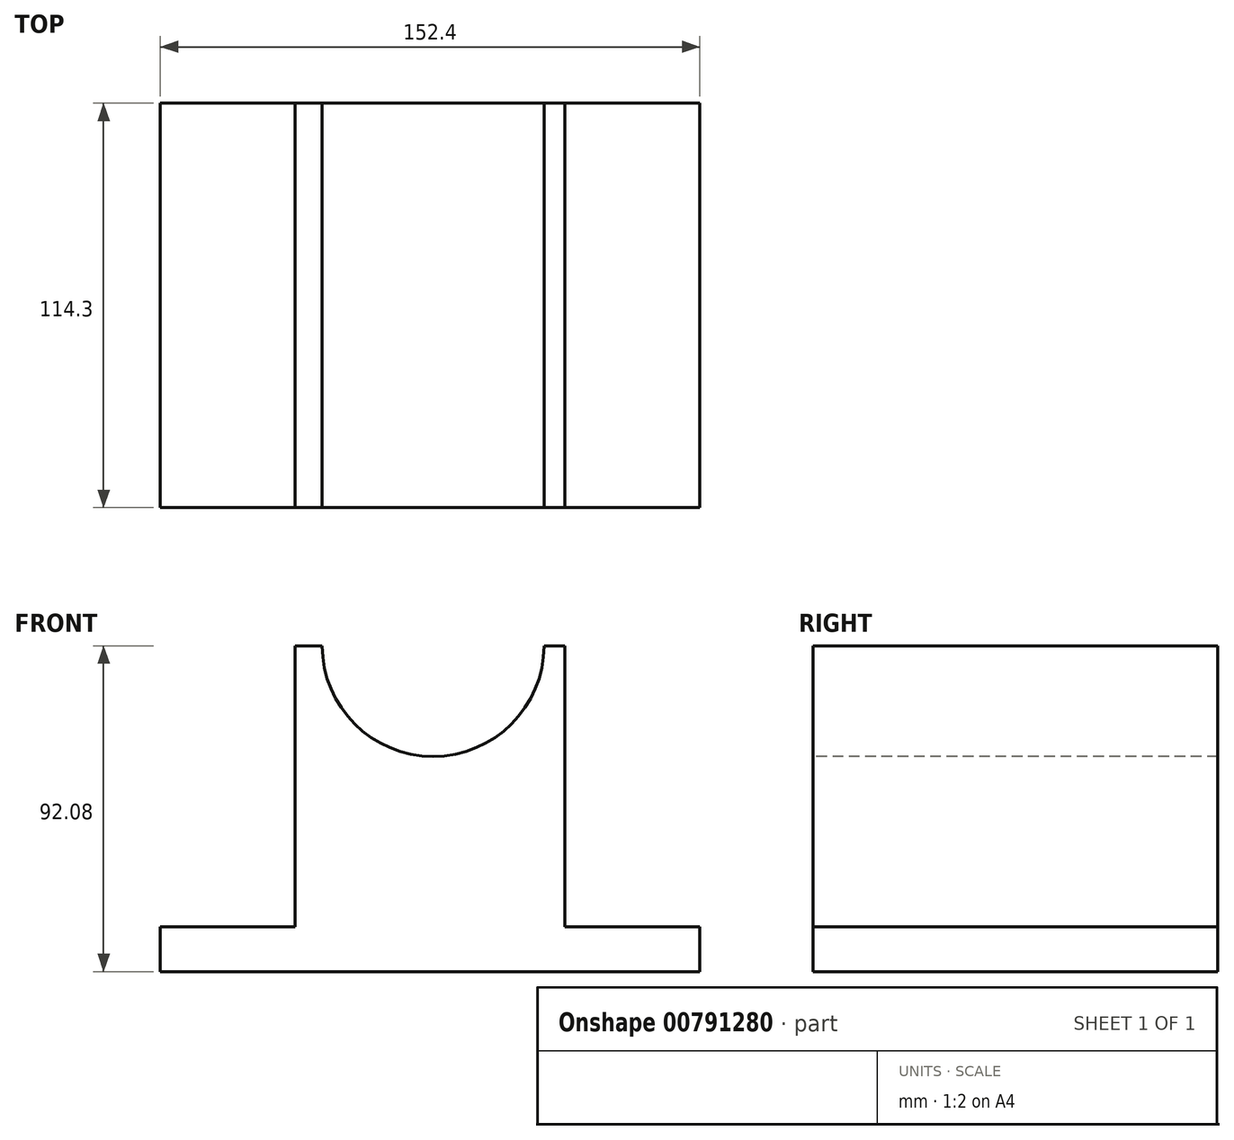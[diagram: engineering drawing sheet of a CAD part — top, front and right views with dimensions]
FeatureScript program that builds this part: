
annotation { "Feature Type Name" : "Feature", "Feature Type Description" : "" }
export const myFeature = defineFeature(function(context is Context, id is Id, definition is map)
    precondition{}
    {
        {
            var Q0;
            Q0=qCreatedBy(makeId("Front.planeOp"),FACE);
            var sketch = newSketch(context, id + "F0", { "sketchPlane" : qUnion([Q0])});
            skLineSegment(sketch, "E0", {"start": v(0, 0) * mm, "end": v(152.4, 0) * mm});
            skLineSegment(sketch, "E1", {"start": v(152.4, 0) * mm, "end": v(152.4, 12.7) * mm});
            skLineSegment(sketch, "E2", {"start": v(152.4, 12.7) * mm, "end": v(114.3, 12.7) * mm});
            skLineSegment(sketch, "E3", {"start": v(114.3, 12.7) * mm, "end": v(114.3, 92.08) * mm});
            skLineSegment(sketch, "E4", {"start": v(114.3, 92.08) * mm, "end": v(38.1, 92.08) * mm});
            skLineSegment(sketch, "E5", {"start": v(38.1, 92.08) * mm, "end": v(38.1, 12.7) * mm});
            skLineSegment(sketch, "E6", {"start": v(38.1, 12.7) * mm, "end": v(0, 12.7) * mm});
            skLineSegment(sketch, "E7", {"start": v(0, 12.7) * mm, "end": v(0, 0) * mm});
            skSolve(sketch);
        }
        {
            var Q0;
            Q0 = qSketchRegion(id + "F0", true);
            extrude(context, id + "F1", {"entities" : qUnion([Q0]), "depth" : 114.3 * mm, "offsetDistance" : 25.4 * mm});
        }
        {
            var Q0;
            Q0=makeQuery(id+"F1.opExtrude","CAP_FACE",FACE,{"disambiguationData":[OSD([sQuery(id+"F0.wireOp",EDGE,"E0"),sQuery(id+"F0.wireOp",EDGE,"E1"),sQuery(id+"F0.wireOp",EDGE,"E2"),sQuery(id+"F0.wireOp",EDGE,"E3"),sQuery(id+"F0.wireOp",EDGE,"E4"),sQuery(id+"F0.wireOp",EDGE,"E5"),sQuery(id+"F0.wireOp",EDGE,"E6"),sQuery(id+"F0.wireOp",EDGE,"E7")])],"isStart":false});
            var sketch = newSketch(context, id + "F2", { "sketchPlane" : qUnion([Q0])});
            skArc(sketch, "E8", {"start": v(45.72, 92.08) * mm, "mid": v(77.06, 60.8) * mm, "end": v(108.4, 92.08) * mm});
            skSolve(sketch);
        }
        {
            var Q0;
            {var subQ0=sQuery(id+"F2.wireOp",EDGE,"E8");Q0=makeQuery(id+"F2.imprint","IMPRINT",FACE,{"disambiguationData":[TD([[makeQuery(id+"F2.imprint","IMPRINT",EDGE,{"derivedFrom":subQ0}),1.0]])]});}
            extrude(context, id + "F3", {"entities" : qUnion([Q0]), "operationType" : NewBodyOperationType.REMOVE, "endBound" : BoundingType.UP_TO_NEXT, "oppositeDirection" : true, "depth" : 25.4 * mm, "offsetDistance" : 25.4 * mm});
        }
    });
